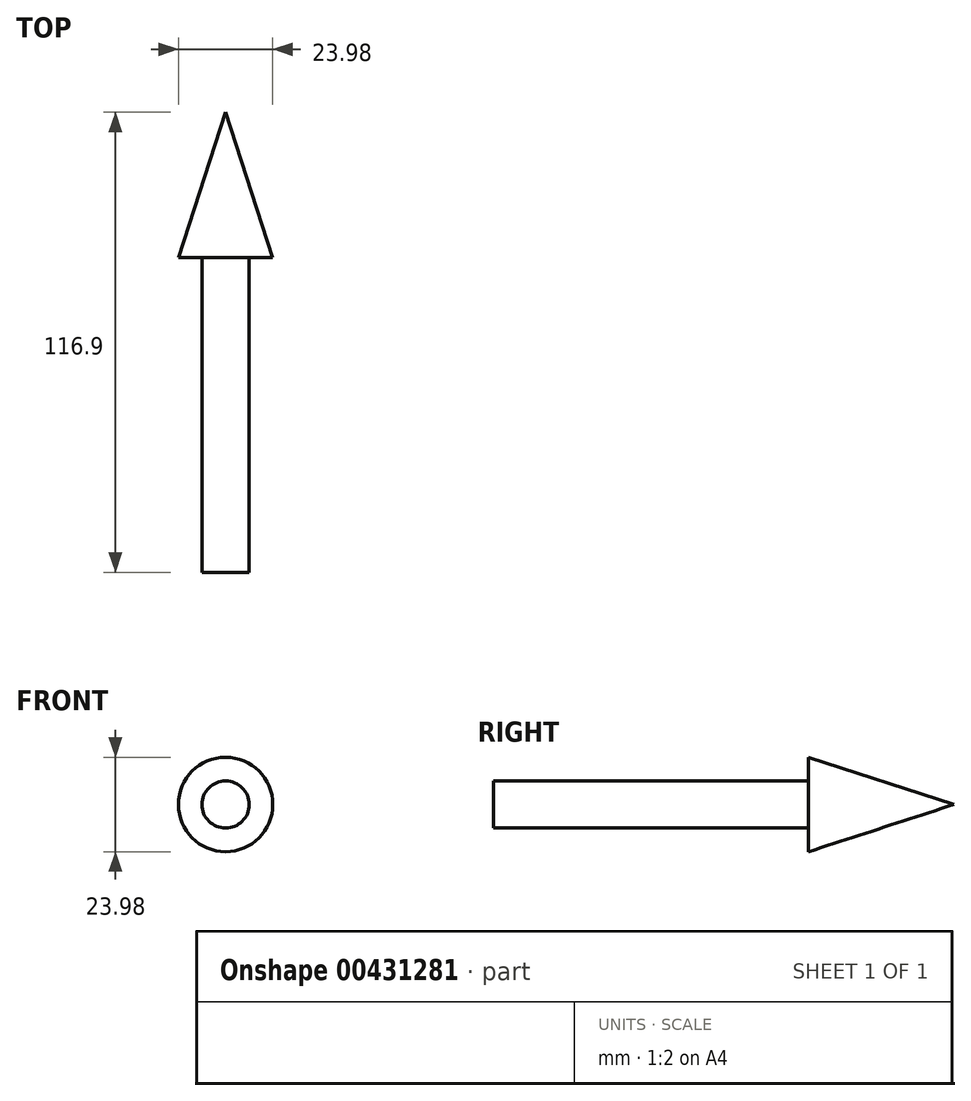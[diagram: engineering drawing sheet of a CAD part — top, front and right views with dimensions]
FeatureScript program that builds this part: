
annotation { "Feature Type Name" : "Feature", "Feature Type Description" : "" }
export const myFeature = defineFeature(function(context is Context, id is Id, definition is map)
    precondition{}
    {
        {
            var Q0;
            Q0=qCreatedBy(makeId("Right.planeOp"),FACE);
            var sketch = newSketch(context, id + "F0", { "sketchPlane" : qUnion([Q0])});
            skLineSegment(sketch, "E0", {"start": v(-53.62, 6) * mm, "end": v(26.38, 6) * mm});
            skLineSegment(sketch, "E1", {"start": v(26.38, 6) * mm, "end": v(26.38, 12) * mm});
            skLineSegment(sketch, "E2", {"start": v(26.38, 12) * mm, "end": v(63.28, 0) * mm});
            skLineSegment(sketch, "E3", {"start": v(63.28, 0) * mm, "end": v(-53.62, 0) * mm});
            skLineSegment(sketch, "E4", {"start": v(-53.62, 0) * mm, "end": v(-53.62, 6) * mm});
            skSolve(sketch);
        }
        {
            var Q0;
            Q0=makeQuery(id+"F0.imprint","IMPRINT",FACE,{"disambiguationData":[TD([[makeQuery(id+"F0.imprint","IMPRINT",EDGE,{"derivedFrom":sQuery(id+"F0.wireOp",EDGE,"E0")}),-1.0]])]});
            var Q1;
            Q1=sQuery(id+"F0.wireOp",EDGE,"E3");
            revolve(context, id + "F1", {"entities" : qUnion([Q0]), "axis" : qUnion([Q1]), "revolveType" : RevolveType.FULL});
        }
    });
